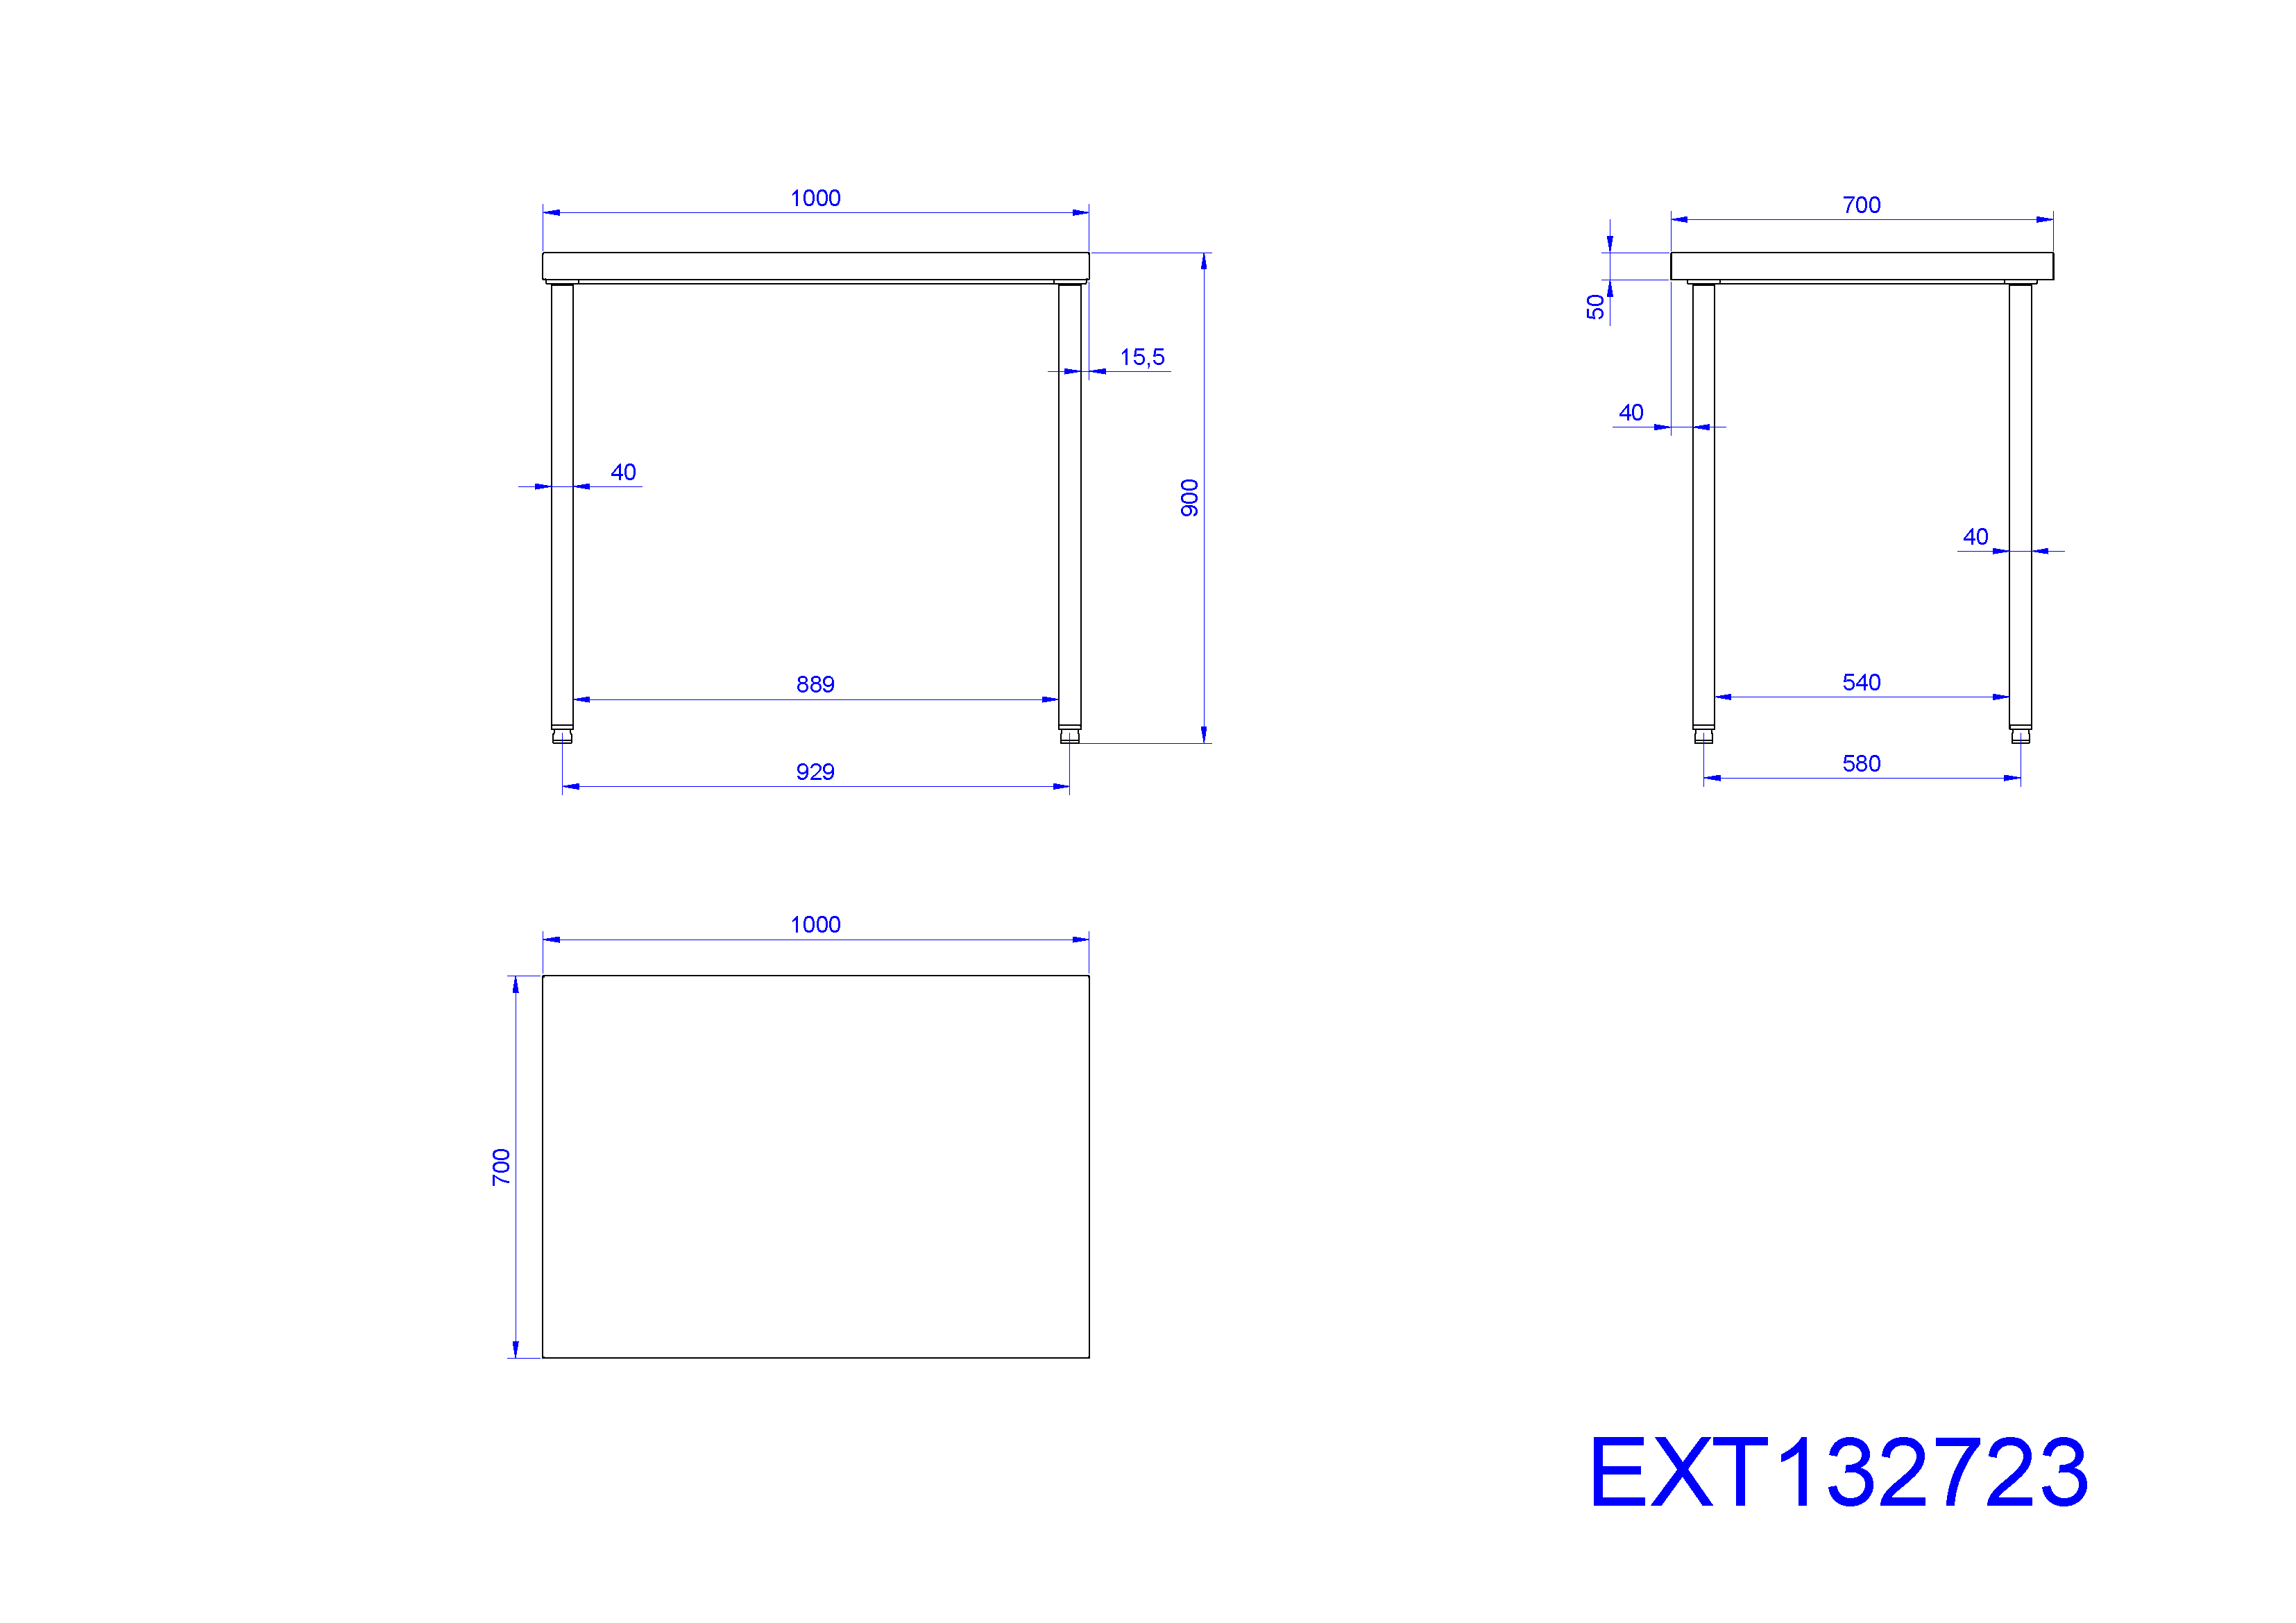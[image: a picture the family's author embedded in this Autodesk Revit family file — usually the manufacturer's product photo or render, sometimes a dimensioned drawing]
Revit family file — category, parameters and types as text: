
# Revit family: QF_ELECTROLUXPROFESSIONAL_133048_TG1000EN
name_source: partatom
category: Attrezzature speciali
units: mm (PartAtom-declared; Revit-internal decimal feet)

## family parameters
Basato su piano di lavoro = No
Condiviso = No
Punto di calcolo locali = No
Quota connettore circolare = Usa diametro
Sempre verticale = Sì
Taglio con vuoti quando caricato = No
Tipo di parte = Normale

## types (1)
- Standard
    Accessory = Sì
    Cold Water Size = 0 mm
    Compressed Air Pressure = 0.0 Pa
    Compressed Air Size = 0 mm
    Compressed Air Volume = 0.0 L/s
    Condensate Return Size = 0 mm
    Cycle = 0 Hz
    Depth Actual = 700 mm  [stored 2.29659 ft]
    Descrizione = WORK TABLE 1000 MM
    Direct Waste Size = 0 mm
    Gas Input Pressure = 0
    Gas KW = 0
    Gas Size = 0 mm
    HP = 0 HP
    Height Actual = 900 mm  [stored 2.95276 ft]
    Hot Water Size = 0 mm
    Item Number = 133048
    Length Actual = 1000 mm  [stored 3.28084 ft]
    Modello = TG1000EN
    Phase = 0
    Produttore = Electrolux Professional
    Prospetto di default = 0 mm  [stored 0 ft]
    Refrigerant Compressor Remote = Sì
    Refrigeration Liquid Line Size = 0 mm  [stored 0 ft]
    Refrigeration Suction Line Size = 0 mm  [stored 0 ft]
    Steam Consumption per Hour = 0
    Steam Supply Maximum Pressure = 0.0 Pa
    Steam Supply Minimum Pressure = 0.0 Pa
    Steam Supply Size = 0 mm
    URL = https://www.electroluxprofessional.com
    URL Manufacturer = https://www.electroluxprofessional.com
    Volts = 0 V
    Watts = 0 W
    Weight = 35.00 kg

note: source unit labels omitted for Gas Input Pressure — the stored unit's dimension contradicts the parameter name (converter mislabeling)

note: [stored X ft] marks values corroborated as IEEE doubles in the binary element streams (Revit-internal decimal feet)

## geometry (parser evidence)
native form markers: Sweep x2
no freeform markers — native parametric forms only
